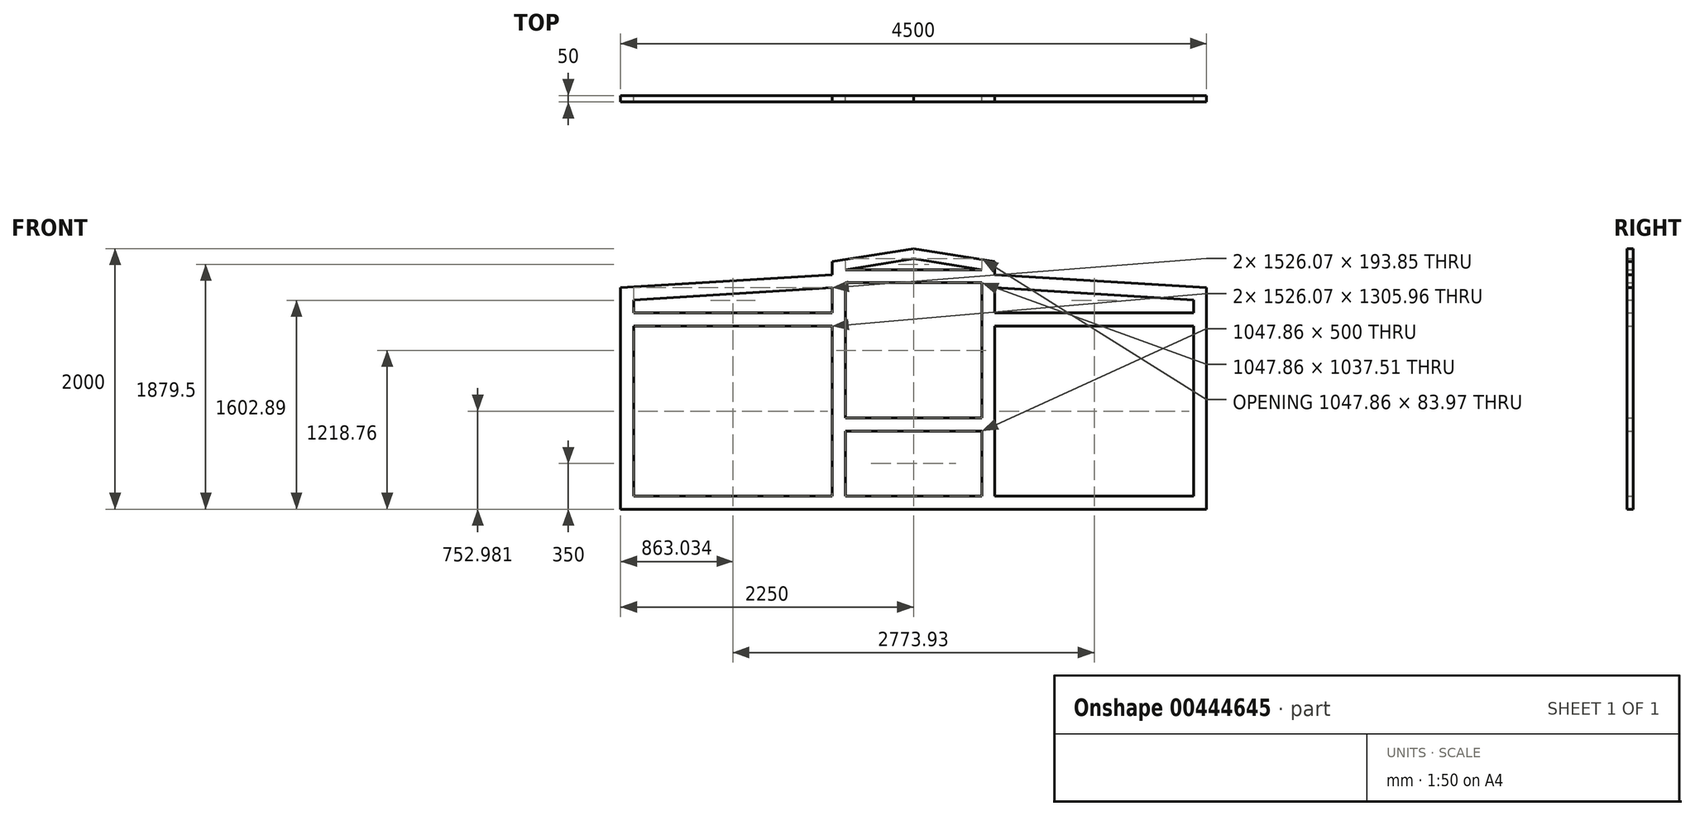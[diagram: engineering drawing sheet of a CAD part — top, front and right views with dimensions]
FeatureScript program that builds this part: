
annotation { "Feature Type Name" : "Feature", "Feature Type Description" : "" }
export const myFeature = defineFeature(function(context is Context, id is Id, definition is map)
    precondition{}
    {
        {
            var Q0;
            Q0=qCreatedBy(makeId("Front.planeOp"),FACE);
            var sketch = newSketch(context, id + "F0", { "sketchPlane" : qUnion([Q0])});
            skLineSegment(sketch, "E0", {"start": v(0, 0) * mm, "end": v(2250, 0) * mm});
            skLineSegment(sketch, "E1", {"start": v(2250, 0) * mm, "end": v(2250, 1700) * mm});
            skLineSegment(sketch, "E2", {"start": v(2250, 1700) * mm, "end": v(623.93, 1800) * mm});
            skLineSegment(sketch, "E3", {"start": v(623.93, 1800) * mm, "end": v(623.93, 1900) * mm});
            skLineSegment(sketch, "E4", {"start": v(623.93, 1900) * mm, "end": v(0, 2000) * mm});
            skLineSegment(sketch, "E5", {"start": v(0, 2000) * mm, "end": v(0, 0) * mm, "construction": true});
            skLineSegment(sketch, "E6", {"start": v(623.93, 1699.81) * mm, "end": v(623.93, 1505.96) * mm});
            skLineSegment(sketch, "E7", {"start": v(523.93, 600) * mm, "end": v(0, 600) * mm});
            skLineSegment(sketch, "E8", {"start": v(0, 1921.49) * mm, "end": v(523.93, 1837.51) * mm});
            skLineSegment(sketch, "E9", {"start": v(523.93, 1737.51) * mm, "end": v(523.93, 700) * mm});
            skLineSegment(sketch, "E10", {"start": v(523.93, 700) * mm, "end": v(0, 700) * mm});
            skLineSegment(sketch, "E11.0", {"start": v(2150, 1605.96) * mm, "end": v(617.8, 1700.19) * mm});
            skLineSegment(sketch, "E11.1", {"start": v(2150, 100) * mm, "end": v(2150, 1405.96) * mm});
            skLineSegment(sketch, "E11.2", {"start": v(0, 100) * mm, "end": v(523.93, 100) * mm});
            skLineSegment(sketch, "E12", {"start": v(623.93, 600) * mm, "end": v(623.93, 100) * mm});
            skLineSegment(sketch, "E13", {"start": v(523.93, 600) * mm, "end": v(523.93, 100) * mm});
            skLineSegment(sketch, "E14", {"start": v(623.93, 1505.96) * mm, "end": v(2150, 1505.96) * mm});
            skLineSegment(sketch, "E15", {"start": v(623.93, 1405.96) * mm, "end": v(2150, 1405.96) * mm});
            skLineSegment(sketch, "E16.trimOffspring", {"start": v(623.93, 1405.96) * mm, "end": v(623.93, 600) * mm});
            skLineSegment(sketch, "E17.trimOffspring", {"start": v(2150, 1505.96) * mm, "end": v(2150, 1605.96) * mm});
            skLineSegment(sketch, "E18.trimOffspring", {"start": v(623.93, 100) * mm, "end": v(2150, 100) * mm});
            skLineSegment(sketch, "E19.MirrorCS", {"start": v(-623.93, 1800) * mm, "end": v(-623.93, 1900) * mm});
            skLineSegment(sketch, "E20.MirrorCS", {"start": v(-2150, 1505.96) * mm, "end": v(-2150, 1605.96) * mm});
            skLineSegment(sketch, "E21.MirrorCS", {"start": v(-623.93, 1699.81) * mm, "end": v(-623.93, 1505.96) * mm});
            skLineSegment(sketch, "E22.MirrorCS", {"start": v(-623.93, 1505.96) * mm, "end": v(-2150, 1505.96) * mm});
            skLineSegment(sketch, "E23.MirrorCS", {"start": v(-623.93, 1405.96) * mm, "end": v(-623.93, 600) * mm});
            skLineSegment(sketch, "E24.MirrorCS", {"start": v(-523.93, 600) * mm, "end": v(-523.93, 100) * mm});
            skLineSegment(sketch, "E25.MirrorCS", {"start": v(-2150, 100) * mm, "end": v(-2150, 1405.96) * mm});
            skLineSegment(sketch, "E26.MirrorCS", {"start": v(0, 0) * mm, "end": v(-2250, 0) * mm});
            skLineSegment(sketch, "E27.MirrorCS", {"start": v(-623.93, 600) * mm, "end": v(-623.93, 100) * mm});
            skLineSegment(sketch, "E28.MirrorCS", {"start": v(-2250, 0) * mm, "end": v(-2250, 1700) * mm});
            skLineSegment(sketch, "E29.MirrorCS", {"start": v(-2250, 1700) * mm, "end": v(-623.93, 1800) * mm});
            skLineSegment(sketch, "E30.MirrorCS", {"start": v(-2150, 1605.96) * mm, "end": v(-617.8, 1700.19) * mm});
            skLineSegment(sketch, "E31.MirrorCS", {"start": v(0, 100) * mm, "end": v(-523.93, 100) * mm});
            skLineSegment(sketch, "E32.MirrorCS", {"start": v(-623.93, 1900) * mm, "end": v(0, 2000) * mm});
            skLineSegment(sketch, "E33.MirrorCS", {"start": v(-523.93, 600) * mm, "end": v(0, 600) * mm});
            skLineSegment(sketch, "E34.MirrorCS", {"start": v(-623.93, 1405.96) * mm, "end": v(-2150, 1405.96) * mm});
            skLineSegment(sketch, "E35.MirrorCS", {"start": v(0, 1921.49) * mm, "end": v(-523.93, 1837.51) * mm});
            skLineSegment(sketch, "E36.MirrorCS", {"start": v(-523.93, 1737.51) * mm, "end": v(-523.93, 700) * mm});
            skLineSegment(sketch, "E37.MirrorCS", {"start": v(-623.93, 100) * mm, "end": v(-2150, 100) * mm});
            skLineSegment(sketch, "E38.MirrorCS", {"start": v(-523.93, 700) * mm, "end": v(0, 700) * mm});
            skLineSegment(sketch, "E39", {"start": v(-523.93, 1837.51) * mm, "end": v(523.93, 1837.51) * mm});
            skLineSegment(sketch, "E40", {"start": v(-523.93, 1737.51) * mm, "end": v(523.93, 1737.51) * mm});
            skSolve(sketch);
        }
        {
            var Q0;
            Q0=qSketchRegion(id+"F0",true);
            extrude(context, id + "F1", {"entities" : qUnion([Q0]), "depth" : 50 * mm});
        }
    });
